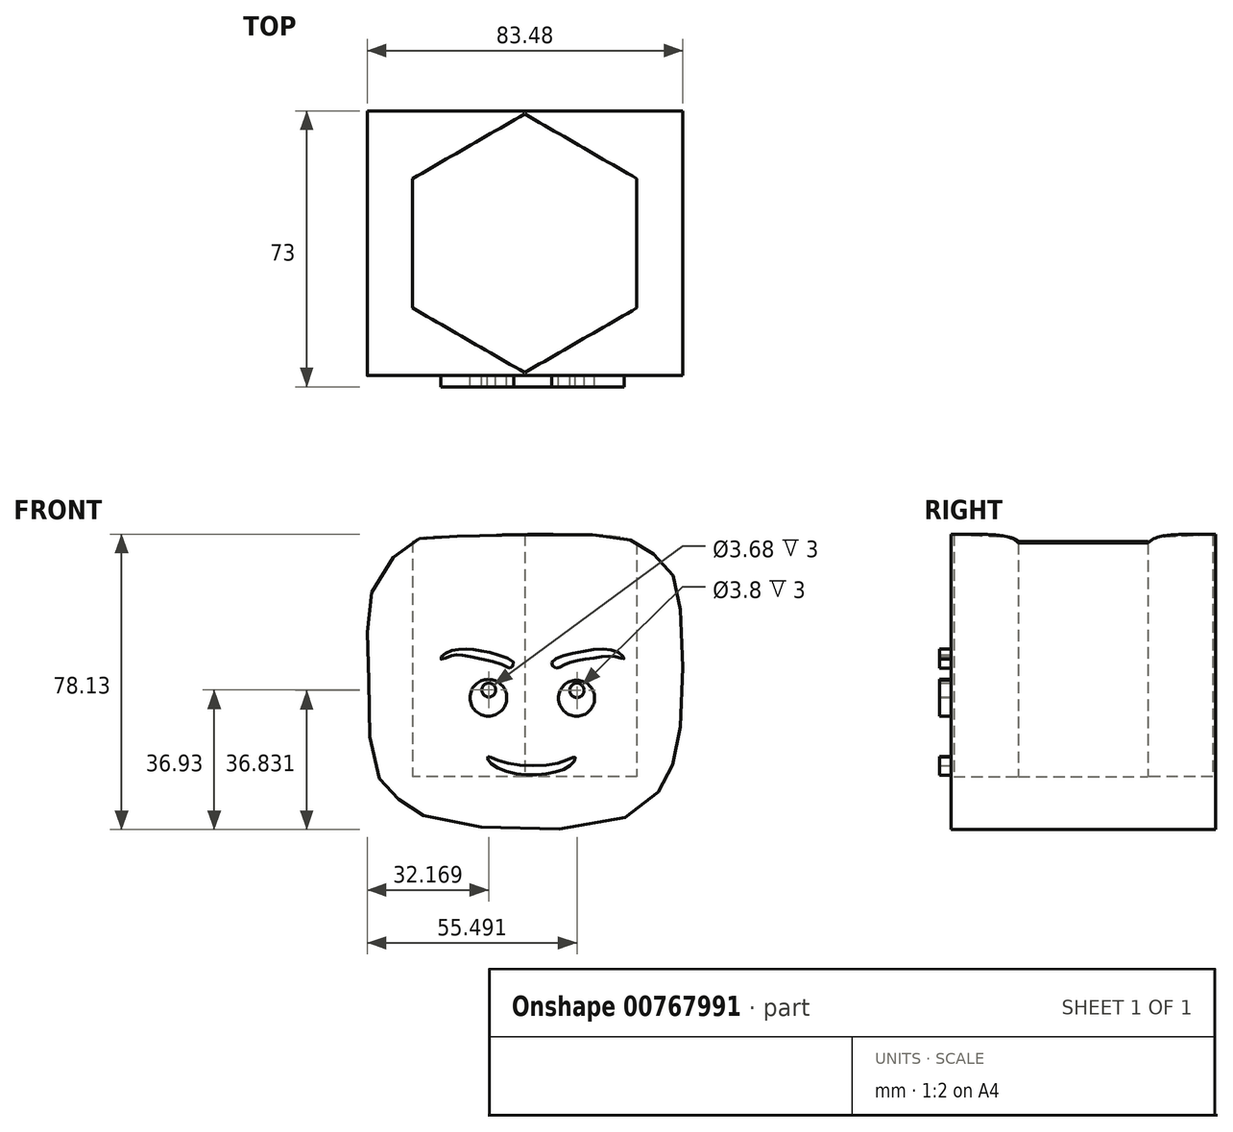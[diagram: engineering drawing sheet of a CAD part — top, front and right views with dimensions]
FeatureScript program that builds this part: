
annotation { "Feature Type Name" : "Feature", "Feature Type Description" : "" }
export const myFeature = defineFeature(function(context is Context, id is Id, definition is map)
    precondition{}
    {
        {
            var Q0;
            Q0=qCreatedBy(makeId("Front.planeOp"),FACE);
            var sketch = newSketch(context, id + "F0", { "sketchPlane" : qUnion([Q0])});
            skFitSpline(sketch, "E0", {"points": [v(-40.42, 20.08) * mm, v(-41.27, 0.98) * mm, v(-39.42, -27) * mm, v(-33.68, -34.37) * mm, v(-25.08, -39.58) * mm, v(25.44, -39.88) * mm, v(37.34, -29.36) * mm, v(40.87, -18.13) * mm, v(41.17, 16.23) * mm, v(37.88, 26.53) * mm, v(30.86, 32.46) * mm, v(22.66, 35.02) * mm, v(-20.44, 34.9) * mm, v(-30.87, 32.86) * mm, v(-40.42, 20.08) * mm]});
            skSolve(sketch);
        }
        {
            var Q0;
            Q0 = qSketchRegion(id + "F0", true);
            extrude(context, id + "F1", {"entities" : qUnion([Q0]), "endBound" : BoundingType.SYMMETRIC, "depth" : 70 * mm, "offsetDistance" : 25 * mm});
        }
        {
            var Q0;
            Q0=makeQuery(id+"F1.opExtrude","CAP_FACE",FACE,{"disambiguationData":[OSD([sQuery(id+"F0.wireOp",EDGE,"E0")])],"isStart":false});
            var sketch = newSketch(context, id + "F2", { "sketchPlane" : qUnion([Q0])});
            skFitSpline(sketch, "E1", {"points": [v(-3.91, 0) * mm, v(-2.9, 1.36) * mm, v(-9.2, 4.13) * mm, v(-15.97, 5.1) * mm, v(-21.21, 3.82) * mm, v(-22.18, 2.46) * mm, v(-19.5, 3.3) * mm, v(-15.67, 3.34) * mm, v(-4.97, 0.52) * mm, v(-3.91, 0) * mm]});
            skFitSpline(sketch, "E2", {"points": [v(8.26, 0) * mm, v(7.13, 1.4) * mm, v(13.88, 4.19) * mm, v(24.27, 4.41) * mm, v(26.27, 2.53) * mm, v(24.38, 3.02) * mm, v(17.8, 2.64) * mm, v(10.67, 1.06) * mm, v(8.26, 0) * mm]});
            skCircle(sketch, "E3", {"center": v(-9.6, -7.82) * mm, "radius": 4.86 * mm});
            skCircle(sketch, "E4", {"center": v(-9.5, -5.74) * mm, "radius": 1.84 * mm});
            skCircle(sketch, "E5", {"center": v(13.72, -7.91) * mm, "radius": 4.77 * mm});
            skCircle(sketch, "E6", {"center": v(13.82, -5.84) * mm, "radius": 1.9 * mm});
            skFitSpline(sketch, "E7", {"points": [v(-9.76, -23.35) * mm, v(-9.54, -24.49) * mm, v(-3.36, -27.69) * mm, v(7.24, -27.69) * mm, v(12.78, -25.06) * mm, v(13.35, -23.5) * mm, v(10, -24.77) * mm, v(-5.7, -24.84) * mm, v(-9.76, -23.35) * mm]});
            skSolve(sketch);
        }
        {
            var Q0;
            Q0 = qSketchRegion(id + "F2", true);
            extrude(context, id + "F3", {"entities" : qUnion([Q0]), "operationType" : NewBodyOperationType.ADD, "depth" : 3 * mm, "offsetDistance" : 25 * mm});
        }
        {
            var Q0;
            Q0=makeQuery(id+"F3.boolean.opBoolean","SPLIT",FACE,{"disambiguationData":[TD([makeQuery(id+"F3.opExtrude","SWEPT_FACE",FACE,{"disambiguationData":[OSD([sQuery(id+"F2.wireOp",EDGE,"E4")])]})])],"derivedFrom":makeQuery(id+"F1.opExtrude","CAP_FACE",FACE,{"disambiguationData":[OSD([sQuery(id+"F0.wireOp",EDGE,"E0")])],"isStart":false})});
            var Q1;
            Q1=makeQuery(id+"F3.boolean.opBoolean","SPLIT",FACE,{"disambiguationData":[TD([makeQuery(id+"F3.opExtrude","SWEPT_FACE",FACE,{"disambiguationData":[OSD([sQuery(id+"F2.wireOp",EDGE,"E6")])]})])],"derivedFrom":makeQuery(id+"F1.opExtrude","CAP_FACE",FACE,{"disambiguationData":[OSD([sQuery(id+"F0.wireOp",EDGE,"E0")])],"isStart":false})});
            extrude(context, id + "F4", {"entities" : qUnion([Q0, Q1]), "operationType" : NewBodyOperationType.ADD, "oppositeDirection" : true, "depth" : 3 * mm, "offsetDistance" : 25 * mm});
        }
        {
            var Q0;
            Q0=qCreatedBy(makeId("Top.planeOp"),FACE);
            var sketch = newSketch(context, id + "F5", { "sketchPlane" : qUnion([Q0])});
            skCircle(sketch, "E8.cCircle", {"center": v(0, 0) * mm, "radius": 29.65 * mm, "construction": true});
            skLineSegment(sketch, "E8.0", {"start": v(-29.65, -17.12) * mm, "end": v(-29.65, 17.12) * mm});
            skLineSegment(sketch, "E8.1", {"start": v(-29.65, 17.12) * mm, "end": v(0, 34.23) * mm});
            skLineSegment(sketch, "E8.2", {"start": v(0, 34.23) * mm, "end": v(29.65, 17.12) * mm});
            skLineSegment(sketch, "E8.3", {"start": v(29.65, 17.12) * mm, "end": v(29.65, -17.12) * mm});
            skLineSegment(sketch, "E8.4", {"start": v(29.65, -17.12) * mm, "end": v(0, -34.23) * mm});
            skLineSegment(sketch, "E8.5", {"start": v(0, -34.23) * mm, "end": v(-29.65, -17.12) * mm});
            skPoint(sketch, "E8.0.midPoint", {"position": v(-29.65, 0) * mm});
            skSolve(sketch);
        }
        {
            var Q0;
            Q0 = qSketchRegion(id + "F5", true);
            extrude(context, id + "F6", {"entities" : qUnion([Q0]), "operationType" : NewBodyOperationType.REMOVE, "endBound" : BoundingType.THROUGH_ALL, "depth" : 25 * mm, "offsetDistance" : 25 * mm});
        }
        {
            var Q0;
            Q0 = qSketchRegion(id + "F5", true);
            extrude(context, id + "F7", {"entities" : qUnion([Q0]), "operationType" : NewBodyOperationType.REMOVE, "oppositeDirection" : true, "depth" : 28.7 * mm, "offsetDistance" : 25 * mm});
        }
    });
